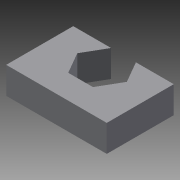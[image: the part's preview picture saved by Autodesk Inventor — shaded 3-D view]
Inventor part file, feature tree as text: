
AUTODESK INVENTOR PART (.ipt)
format: ipt  version: 2015 SP1 (Build 190203100, 203)  size: 78,336 bytes
history: native  units: mm
features: extrude x1, sketch x1
ambient origin geometry x8: Origin, YZ Plane, XZ Plane, XY Plane, X Axis, Y Axis, Z Axis, Center Point
bodies: Solid1 (feature_tree)
feature tree (2):
  extrude  "Extrusion1"  Depth=20.0mm
  sketch  "Sketch1"  dims[d0=30.0mm d1=20.0mm d2=12.8mm d3=0.0mm d4=15.0mm d5=8.0mm d6=0.0mm]
